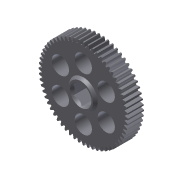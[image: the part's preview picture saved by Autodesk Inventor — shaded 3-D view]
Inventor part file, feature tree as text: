
AUTODESK INVENTOR PART (.ipt)
format: ipt  version: 2011 (Build 150239000, 239)  size: 470,016 bytes
history: native  units: mm (DEFAULTED — no unit token found)
features: sketch x6, other x4, extrude x4, plane x3, revolve x1, pattern_circular x1, projected_geometry x1
ambient origin geometry x8: Origin, YZ Plane, XZ Plane, XY Plane, X Axis, Y Axis, Z Axis, Center Point
bodies: Solid1 (feature_tree)
feature tree (20):
  other  "Gear 60T 32dp 375hex"
  extrude  "Extrusion1"  Depth=8.763mm TaperAngle=0.0deg
  plane  "Work Plane1"
  plane  "Work Plane2"
  plane  "Work Plane3"
  other  "Spur Gear"
  extrude  "Extrusion2"  Depth=76.2mm TaperAngle=0.0deg
  extrude  "Extrusion3"  TaperAngle=0.0deg  [1 undecoded]
  revolve  "Revolution1"  [1 undecoded]
  extrude  "Extrusion4"  Depth=15.875mm
  pattern_circular  "Circular Pattern1"  [2 undecoded]
  sketch  "Sketch1"  dims[d0=49.2125mm d1=8.763mm d2=0.0mm]
  sketch  "Sketch2"  dims[d3=47.625mm d4=76.2mm d5=0.0mm]
  other  "Srf1"
  sketch  "Sketch3"  dims[d6=0.0mm d7=0.523599mm d9=0.0mm]
  sketch  "Sketch4"  dims[d14=0.0mm d15=47.625mm d16=0.0mm]
  sketch  "Sketch5"  dims[d17=0.0mm d18=0.0mm d19=47.625mm d20=15.875mm]
  sketch  "Sketch6"  dims[d21=1.397mm d22=0.0mm d23=9.525mm d24=1.397mm d25=0.0mm d26=1.143mm d27=0.889mm d28=8.850565mm d29=90.0deg d30=9.525mm d31=14.605mm d32=1.397mm d33=0.0mm d34=60.0mm d35=360.0deg]
  other  "Pitch Diameter"
  projected_geometry  "Project Cut Edges1"
note: 4 required parameter values undecoded (feature->parameter linkage not recoverable at this tier; creation-order binding heuristic only, values carry confidence <= 0.55)